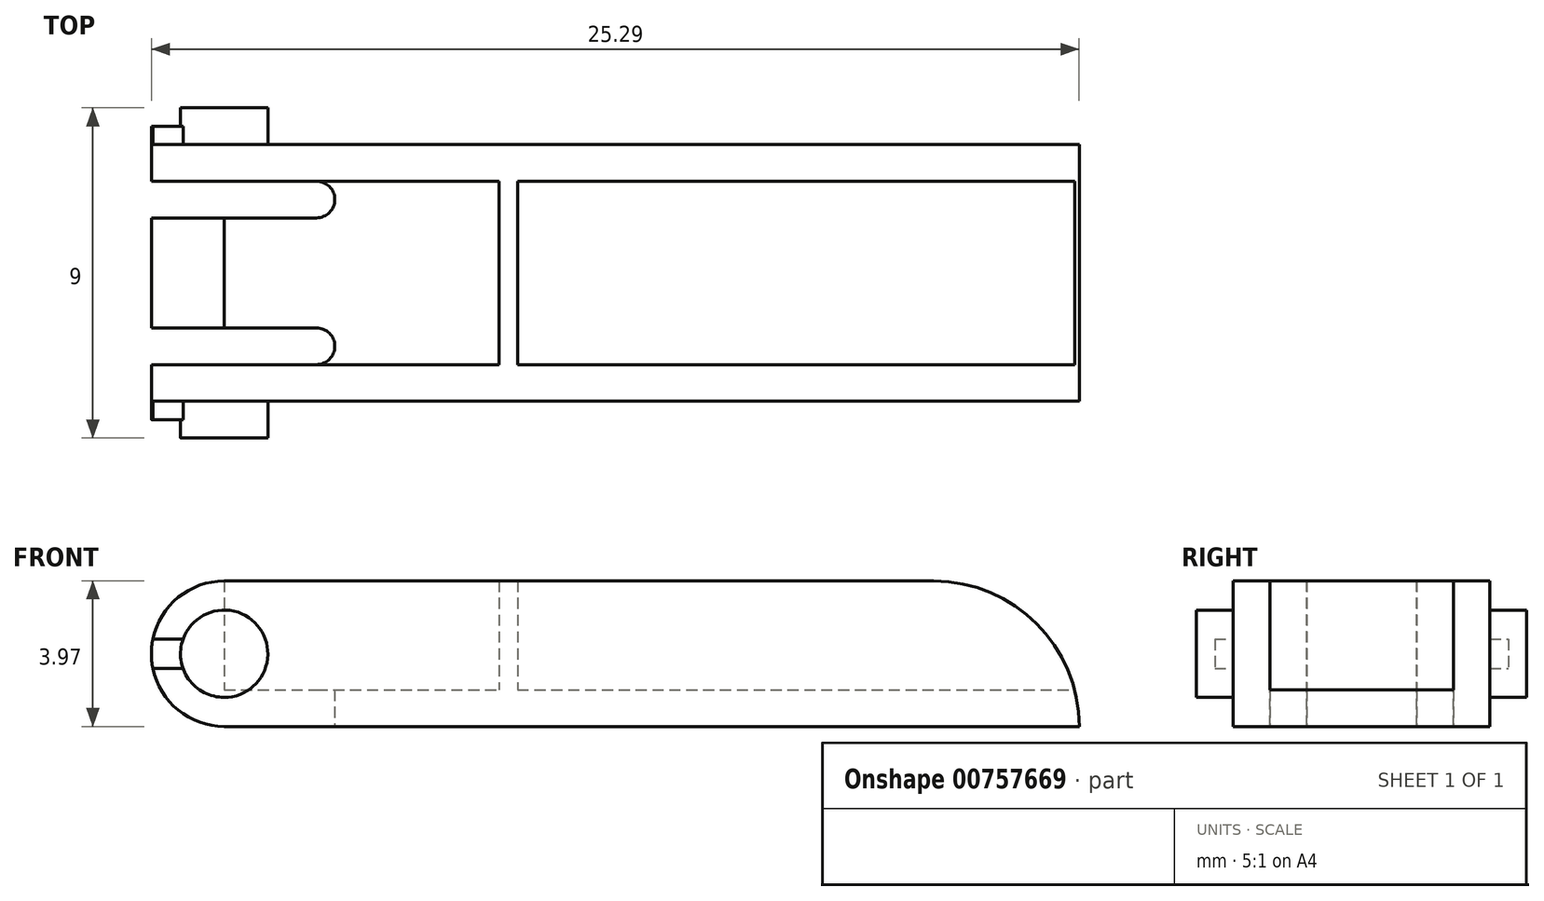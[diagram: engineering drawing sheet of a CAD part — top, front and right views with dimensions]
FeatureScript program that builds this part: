
annotation { "Feature Type Name" : "Feature", "Feature Type Description" : "" }
export const myFeature = defineFeature(function(context is Context, id is Id, definition is map)
    precondition{}
    {
        {
            var Q0;
            Q0=qCreatedBy(makeId("Front.planeOp"),FACE);
            var sketch = newSketch(context, id + "F0", { "sketchPlane" : qUnion([Q0])});
            skLineSegment(sketch, "E0.left", {"start": v(0, 0) * mm, "end": v(23.31, 0) * mm});
            skLineSegment(sketch, "E0.right", {"start": v(0, 3.97) * mm, "end": v(19.35, 3.97) * mm});
            skPoint(sketch, "E0.middle", {"position": v(0, 0) * mm});
            skLineSegment(sketch, "E1", {"start": v(0, 0) * mm, "end": v(0, 3.97) * mm, "construction": true});
            skCircle(sketch, "E2", {"center": v(0, 1.98) * mm, "radius": 1.98 * mm});
            skCircle(sketch, "E3", {"center": v(0, 1.98) * mm, "radius": 1.2 * mm});
            skLineSegment(sketch, "E4", {"start": v(-1.98, 1.98) * mm, "end": v(1.98, 1.98) * mm, "construction": true});
            skLineSegment(sketch, "E5", {"start": v(-1.94, 1.59) * mm, "end": v(-1.12, 1.59) * mm});
            skLineSegment(sketch, "E6.MirrorCS", {"start": v(-1.94, 2.38) * mm, "end": v(-1.12, 2.38) * mm});
            skPoint(sketch, "E7", {"position": v(-1.98, 1.98) * mm});
            skArc(sketch, "E8", {"start": v(23.31, 0) * mm, "mid": v(22.15, 2.8) * mm, "end": v(19.35, 3.97) * mm});
            skSolve(sketch);
        }
        {
            var Q0;
            Q0=qSketchRegion(id+"F0",true);
            extrude(context, id + "F1", {"entities" : qUnion([Q0]), "endBound" : BoundingType.SYMMETRIC, "depth" : 7 * mm, "offsetDistance" : 25 * mm});
        }
        {
            var Q0;
            {var subQ0=sQuery(id+"F0.wireOp",EDGE,"E3");var subQ1=makeQuery(id+"F0.imprint","INTERSECT",VERTEX,{"derivedFrom":[subQ0,sQuery(id+"F0.wireOp",EDGE,"E5")]});Q0=makeQuery(id+"F0.imprint","IMPRINT",FACE,{"disambiguationData":[TD([[makeQuery(id+"F0.imprint","IMPRINT",EDGE,{"disambiguationData":[TD([[subQ1,1.0]])],"derivedFrom":subQ0}),1.0]])]});}
            extrude(context, id + "F2", {"entities" : qUnion([Q0]), "operationType" : NewBodyOperationType.ADD, "endBound" : BoundingType.SYMMETRIC, "depth" : 9 * mm, "offsetDistance" : 25 * mm});
        }
        {
            var Q0;
            {var subQ0=sQuery(id+"F0.wireOp",EDGE,"E5");Q0=makeQuery(id+"F0.imprint","IMPRINT",FACE,{"disambiguationData":[TD([[makeQuery(id+"F0.imprint","IMPRINT",EDGE,{"derivedFrom":subQ0}),1.0]])]});}
            extrude(context, id + "F3", {"entities" : qUnion([Q0]), "operationType" : NewBodyOperationType.ADD, "endBound" : BoundingType.SYMMETRIC, "depth" : 8 * mm, "offsetDistance" : 25 * mm});
        }
        {
            var Q0;
            Q0=qCreatedBy(makeId("Top.planeOp"),FACE);
            var sketch = newSketch(context, id + "F4", { "sketchPlane" : qUnion([Q0])});
            skLineSegment(sketch, "E9", {"start": v(-1.98, -2.5) * mm, "end": v(2.52, -2.5) * mm});
            skLineSegment(sketch, "E10", {"start": v(-1.98, -3.5) * mm, "end": v(-1.98, 3.5) * mm, "construction": true});
            skLineSegment(sketch, "E11.0", {"start": v(-1.98, -3.5) * mm, "end": v(0, -3.5) * mm, "construction": true});
            skPoint(sketch, "E12.orphan", {"position": v(0, -3.5) * mm});
            skLineSegment(sketch, "E13.0", {"start": v(-1.98, 3.5) * mm, "end": v(0, 3.5) * mm, "construction": true});
            skPoint(sketch, "E14.orphan", {"position": v(0, 3.5) * mm});
            skLineSegment(sketch, "E15", {"start": v(0, 3.5) * mm, "end": v(0, -3.5) * mm, "construction": true});
            skLineSegment(sketch, "E16", {"start": v(-1.98, -2) * mm, "end": v(0, -2) * mm, "construction": true});
            skLineSegment(sketch, "E17.MirrorCS", {"start": v(-1.98, -1.5) * mm, "end": v(2.52, -1.5) * mm});
            skArc(sketch, "E18", {"start": v(2.52, -2.5) * mm, "mid": v(3.02, -2) * mm, "end": v(2.52, -1.5) * mm});
            skLineSegment(sketch, "E19.MirrorCS", {"start": v(-1.98, 1.5) * mm, "end": v(2.52, 1.5) * mm});
            skArc(sketch, "E20.MirrorCS", {"start": v(2.52, 2.5) * mm, "mid": v(3.02, 2) * mm, "end": v(2.52, 1.5) * mm});
            skLineSegment(sketch, "E21.MirrorCS", {"start": v(-1.98, 2.5) * mm, "end": v(2.52, 2.5) * mm});
            skLineSegment(sketch, "E22", {"start": v(-1.98, -1.5) * mm, "end": v(-1.98, -2.5) * mm});
            skLineSegment(sketch, "E23.MirrorCS", {"start": v(-1.98, 1.5) * mm, "end": v(-1.98, 2.5) * mm});
            skLineSegment(sketch, "E24.bottom", {"start": v(0, -2.5) * mm, "end": v(7.5, -2.5) * mm});
            skLineSegment(sketch, "E24.top", {"start": v(0, 2.5) * mm, "end": v(7.5, 2.5) * mm});
            skLineSegment(sketch, "E24.left", {"start": v(0, -2.5) * mm, "end": v(0, 2.5) * mm});
            skLineSegment(sketch, "E24.right", {"start": v(7.5, -2.5) * mm, "end": v(7.5, 2.5) * mm});
            skLineSegment(sketch, "E25.bottom", {"start": v(8, -2.5) * mm, "end": v(23.31, -2.5) * mm});
            skLineSegment(sketch, "E25.top", {"start": v(8, 2.5) * mm, "end": v(23.31, 2.5) * mm});
            skLineSegment(sketch, "E25.left", {"start": v(8, -2.5) * mm, "end": v(8, 2.5) * mm});
            skLineSegment(sketch, "E25.right", {"start": v(23.31, -2.5) * mm, "end": v(23.31, 2.5) * mm});
            skLineSegment(sketch, "E26.0", {"start": v(23.31, -3.5) * mm, "end": v(23.31, 3.5) * mm, "construction": true});
            skSolve(sketch);
        }
        {
            var Q0;
            Q0=makeQuery(id+"F4.imprint","IMPRINT",FACE,{"disambiguationData":[TD([[makeQuery(id+"F4.imprint","IMPRINT",EDGE,{"derivedFrom":sQuery(id+"F4.wireOp",EDGE,"E19.MirrorCS")}),1.0]])]});
            var Q1;
            Q1=makeQuery(id+"F4.imprint","IMPRINT",FACE,{"disambiguationData":[TD([[makeQuery(id+"F4.imprint","IMPRINT",EDGE,{"derivedFrom":sQuery(id+"F4.wireOp",EDGE,"E9")}),1.0]])]});
            var Q2;
            {var subQ0=sQuery(id+"F4.wireOp",EDGE,"E18");Q2=makeQuery(id+"F4.imprint","IMPRINT",FACE,{"disambiguationData":[TD([[makeQuery(id+"F4.imprint","IMPRINT",EDGE,{"derivedFrom":subQ0}),1.0]])]});}
            extrude(context, id + "F5", {"entities" : qUnion([Q0, Q1, Q2]), "operationType" : NewBodyOperationType.REMOVE, "depth" : 25 * mm, "offsetDistance" : 25 * mm});
        }
        {
            var Q0;
            {var subQ5=sQuery(id+"F4.wireOp",EDGE,"E18");Q0=makeQuery(id+"F4.imprint","IMPRINT",FACE,{"disambiguationData":[TD([[makeQuery(id+"F4.imprint","IMPRINT",EDGE,{"derivedFrom":subQ5}),-1.0]])]});}
            var Q1;
            Q1=makeQuery(id+"F4.imprint","IMPRINT",FACE,{"disambiguationData":[TD([[makeQuery(id+"F4.imprint","IMPRINT",EDGE,{"derivedFrom":sQuery(id+"F4.wireOp",EDGE,"E25.bottom")}),1.0]])]});
            extrude(context, id + "F6", {"entities" : qUnion([Q0, Q1]), "operationType" : NewBodyOperationType.REMOVE, "endBound" : BoundingType.THROUGH_ALL, "depth" : 10 * mm, "offsetDistance" : 25 * mm, "hasSecondDirection" : true, "secondDirectionOppositeDirection" : false, "secondDirectionDepth" : 1 * mm});
        }
    });
